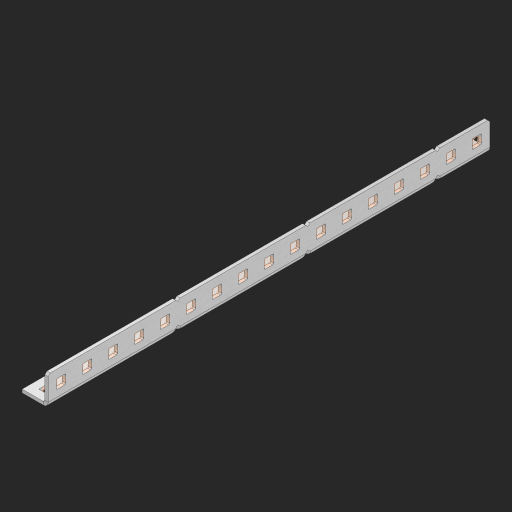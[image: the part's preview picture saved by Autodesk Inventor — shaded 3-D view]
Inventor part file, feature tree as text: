
AUTODESK INVENTOR PART (.ipt)
format: ipt  version: 2023 (Build 270158000, 158)  size: 713,728 bytes
history: native  units: in
note: dims shown in document units (in); Inventor stores cm internally (conversion verified against a paired STEP export)
features: other x39, extrude x33, sheet_metal_op x10, sketch x8, mirror x1, pattern_linear x1, chamfer x1
ambient origin geometry x8: Origin, YZ Plane, XZ Plane, XY Plane, X Axis, Y Axis, Z Axis, Center Point
bodies: Solid1 (feature_tree), Body (feature_tree)
feature tree (93):
  other  "Flange Pattern Plane"
  sheet_metal_op  "Flange Pattern"
  sheet_metal_op  "Body Pattern"
  other  "Arc Length"
  mirror  "Notch Mirror"
  pattern_linear  "Notch Pattern"  Spacing1=0.25in  [1 undecoded]
  chamfer  "End Chamfer"
  extrude  "Half Cut"  Depth=0.0625in
  sketch  "Sketch1"  dims[d0=1.5in]
  other  "Plate1"
  sketch  "Sketch2"  dims[d1=8.5in]
  other  "Plate2"
  sheet_metal_op  "Bend1"
  sheet_metal_op  "Corner1"
  sketch  "Sketch3"  dims[d2=0.0625in]
  other  "Flange Pattern Sketch"
  sketch  "Sketch7"  dims[d3=0.0625in]
  other  "Srf1"
  other  "Srf2"
  sketch  "Sketch8"  dims[d4=0.0312in]
  sketch  "Sketch9"  dims[d5=0.125in]
  other  "Srf91"
  sheet_metal_op  "Body Pattern Sketch"
  other  "Srf92"
  sketch  "Sketch13"  dims[d6=0.0625in]
  sketch  "Sketch14"  dims[d7=0.5in d8=90.0deg d9=0.0312in d10=0.25in d11=0.0625in d12=0.0625in d16=0.182in d17=0.02in d18=0.0625in d19=0.0in d20=0.25in d21=0.25in d46=0.172in d47=1.0in d48=0.0in d49=0.182in d50=0.02in d51=0.25in d52=0.25in d53=0.0625in d54=0.0in d55=0.172in d56=1.0in d57=0.0in d60=6.6929in d62=0.5in d63=0.3937in d65=0.5in d85=0.1473in d86=0.1782in d88=0.04in d89=0.0625in d90=0.0in d91=0.04in d92=0.0491in d95=2.5in d96=0.04in d97=0.25in d98=45.0deg d101=0.0in d102=2.497in d131=0.5in d132=6.6929in d134=0.5in d139=0.5in]
  other  "Srf856"
  other  "Srf1310"
  other  "Srf1311"
  other  "Srf1312"
  other  "Srf1376"
  other  "Srf1377"
  other  "Srf1728"
  other  "Srf1755"
  other  "Srf1878"
  other  "Srf1879"
  other  "Srf1880"
  other  "Srf1881"
  other  "Srf1882"
  other  "Srf1883"
  other  "Srf1884"
  other  "Srf1885"
  other  "Srf1886"
  other  "Srf1887"
  other  "Srf1888"
  other  "Srf1942"
  other  "Srf1943"
  other  "Srf1944"
  other  "Srf1945"
  other  "Srf1946"
  other  "Srf1947"
  other  "Srf1948"
  other  "Srf1949"
  other  "Srf1950"
  other  "Srf1951"
  other  "Srf1952"
  sheet_metal_op  "Flange Stamp"
  sheet_metal_op  "Flange Circle"
  sheet_metal_op  "Body Stamp"
  sheet_metal_op  "Body Circle"
  sheet_metal_op  "Notch"
  extrude  "ExtrusionSrf2"  Depth=0.0625in
  extrude  "ExtrusionSrf92"  Depth=0.5in
  extrude  "ExtrusionSrf856"  Depth=0.02in
  extrude  "ExtrusionSrf1310"  Depth=0.0625in
  extrude  "ExtrusionSrf1311"  TaperAngle=0.0deg  [1 undecoded]
  extrude  "ExtrusionSrf1312"  Depth=0.5in
  extrude  "ExtrusionSrf1376"  Depth=0.5in
  extrude  "ExtrusionSrf1377"  Depth=0.5in
  extrude  "ExtrusionSrf1728"  Depth=0.5in TaperAngle=0.0deg
  extrude  "ExtrusionSrf1755"  Depth=0.5in
  extrude  "ExtrusionSrf1878"  Depth=0.02in
  extrude  "ExtrusionSrf1879"  Depth=0.5in
  extrude  "ExtrusionSrf1880"  Depth=0.5in
  extrude  "ExtrusionSrf1881"  Depth=0.0625in
  extrude  "ExtrusionSrf1882"  TaperAngle=0.0deg  [1 undecoded]
  extrude  "ExtrusionSrf1883"  Depth=0.5in
  extrude  "ExtrusionSrf1884"  Depth=0.5in TaperAngle=0.0deg
  extrude  "ExtrusionSrf1885"  Depth=0.5in
  extrude  "ExtrusionSrf1886"  Depth=0.5in
  extrude  "ExtrusionSrf1887"  Depth=0.5in
  extrude  "ExtrusionSrf1888"  Depth=0.5in
  extrude  "ExtrusionSrf1942"  Depth=0.5in
  extrude  "ExtrusionSrf1943"  Depth=0.0625in
  extrude  "ExtrusionSrf1944"  TaperAngle=0.0deg  [1 undecoded]
  extrude  "ExtrusionSrf1945"  Depth=0.5in
  extrude  "ExtrusionSrf1946"  Depth=0.5in
  extrude  "ExtrusionSrf1947"  Depth=0.5in
  extrude  "ExtrusionSrf1948"  Depth=0.5in TaperAngle=45.0deg
  extrude  "ExtrusionSrf1949"  TaperAngle=0.0deg  [1 undecoded]
  extrude  "ExtrusionSrf1950"  Depth=0.5in
  extrude  "ExtrusionSrf1951"  Depth=0.5in
  extrude  "ExtrusionSrf1952"  Depth=0.5in
note: 5 required parameter values undecoded (feature->parameter linkage not recoverable at this tier; creation-order binding heuristic only, values carry confidence <= 0.55)
